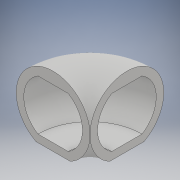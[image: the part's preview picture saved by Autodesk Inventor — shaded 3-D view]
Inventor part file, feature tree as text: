
AUTODESK INVENTOR PART (.ipt)
format: ipt  version: 2017 (Build 210142000, 142)  size: 164,864 bytes
history: native  units: in
note: dims shown in document units (in); Inventor stores cm internally (conversion verified against a paired STEP export)
features: other x1, sketch x1
ambient origin geometry x8: Origin, YZ Plane, XZ Plane, XY Plane, X Axis, Y Axis, Z Axis, Center Point
bodies: Solid1 (feature_tree)
feature tree (2):
  other  "corridor"
  sketch  "Sketch1"  dims[d0=6.6667in d1=4.0in d2=90.0deg d11=1.0in]
